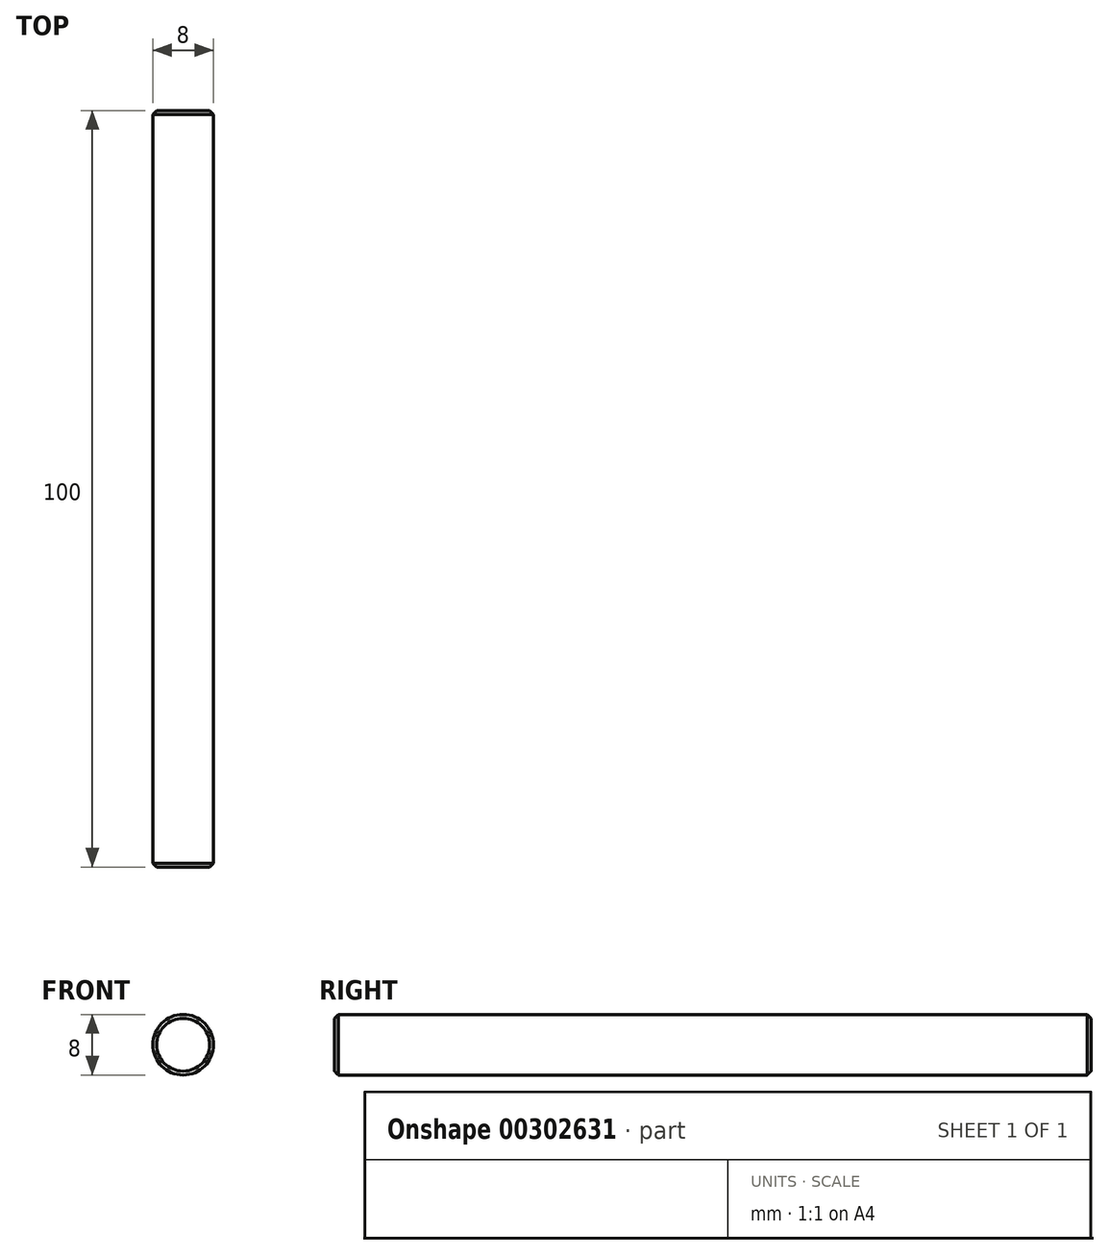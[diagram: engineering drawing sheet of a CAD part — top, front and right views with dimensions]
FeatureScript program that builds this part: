
annotation { "Feature Type Name" : "Feature", "Feature Type Description" : "" }
export const myFeature = defineFeature(function(context is Context, id is Id, definition is map)
    precondition{}
    {
        {
            var Q0;
            Q0=qCreatedBy(makeId("Front.planeOp"),FACE);
            var sketch = newSketch(context, id + "F0", { "sketchPlane" : qUnion([Q0])});
            skCircle(sketch, "E0", {"center": v(0, 0) * mm, "radius": 4 * mm});
            skSolve(sketch);
        }
        {
            var Q0;
            Q0 = qSketchRegion(id + "F0", true);
            extrude(context, id + "F1", {"entities" : qUnion([Q0]), "depth" : 100 * mm});
        }
        {
            var Q0;
            Q0=makeQuery(id+"F1.opExtrude","CAP_EDGE",EDGE,{"disambiguationData":[OSD([sQuery(id+"F0.wireOp",EDGE,"E0")])],"isStart":true});
            chamfer(context, id + "F2", {"entities" : qUnion([Q0]), "width" : 0.5 * mm, "tangentPropagation" : true});
        }
        {
            var Q0;
            Q0=makeQuery(id+"F1.opExtrude","CAP_EDGE",EDGE,{"disambiguationData":[OSD([sQuery(id+"F0.wireOp",EDGE,"E0")])],"isStart":false});
            chamfer(context, id + "F3", {"entities" : qUnion([Q0]), "width" : 0.5 * mm, "tangentPropagation" : true});
        }
    });
